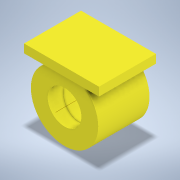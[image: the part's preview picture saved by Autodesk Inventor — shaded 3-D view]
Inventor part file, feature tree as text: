
AUTODESK INVENTOR PART (.ipt)
format: ipt  version: 2020 (Build 240168000, 168)  size: 262,144 bytes
history: native  units: in
note: dims shown in document units (in); Inventor stores cm internally (conversion verified against a paired STEP export)
features: sketch x3, extrude x2, plane x1, other x1, helix x1
ambient origin geometry x8: Origin, YZ Plane, XZ Plane, XY Plane, X Axis, Y Axis, Z Axis, Center Point
bodies: Solid1 (feature_tree)
feature tree (8):
  extrude  "Extrusion1"  Depth=1.9685in
  plane  "Work Plane1"
  extrude  "Extrusion2"  Depth=1.9685in
  sketch  "Sketch3"  dims[d7=0.1969in d8=1.0in d9=1.0in d10=1.1811in d11=0.0in d12=90.0deg d13=90.0deg d14=0.0in d15=0.0in]
  other  "Work Axis1"
  helix  "Coil1"  [1 undecoded]
  sketch  "Sketch1"  dims[d0=3.937in d1=1.9685in]
  sketch  "Sketch2"  dims[d2=3.0in d3=0.0in d4=1.9685in d5=0.5in d6=0.0in]
note: 1 required parameter value undecoded (feature->parameter linkage not recoverable at this tier; creation-order binding heuristic only, values carry confidence <= 0.55)
